# Revit family: VRO-SMK
name_source: partatom
category: Lighting Fixtures
units: mm (PartAtom-declared; Revit-internal decimal feet)

## family parameters
Cut with Voids When Loaded = Yes
Host = Face
Light Source = Yes
Maintain Annotation Orientation = No
Part Type = Normal
Room Calculation Point = No
Round Connector Dimension = Use Diameter
Shared = No

## types (4) — shared parameters
Beam Angle = 0.00°
CRI = 90
Color Filter = 16777215
Default Elevation = 0' - 0"
Dimming Lamp Color Temperature Shift = <None>
Input Voltage = 120-277V
Lamp = LED
Load Classification = Lighting
Manufacturer = Above All Lighting
Power Factor = 0.9
Tilt Angle = 90.00°

## per-type parameters (varying)
| type | 1/2 D | Model | Photometric Web File | Wattage Comments |
| VRO-32W-4000K-SMK | 0' - 11 13/16" | VRO-3624-40901-SMK-WH | VRO_3624_40901_WH.ies | 32W |
| VRO-40W-3000K-SMK | 1' - 5 11/16" | VRO-4035-30901-SMK-WH | VRO_4035_30901_WH.ies | 40W |
| VRO-70W-3000K-SMK | 1' - 11 19/32" | VRO-7047-30901-SMK-WH | VRO_7047_30901_WH.ies | 70W |
| VRO-80W-3000K-SMK | 2' - 5 9/16" | VRO-8059-30901-SMK-WH | VRO_8059_30901_WH.ies | 80W |

## geometry (parser evidence)
native form markers: Sweep x2
no freeform markers — native parametric forms only
